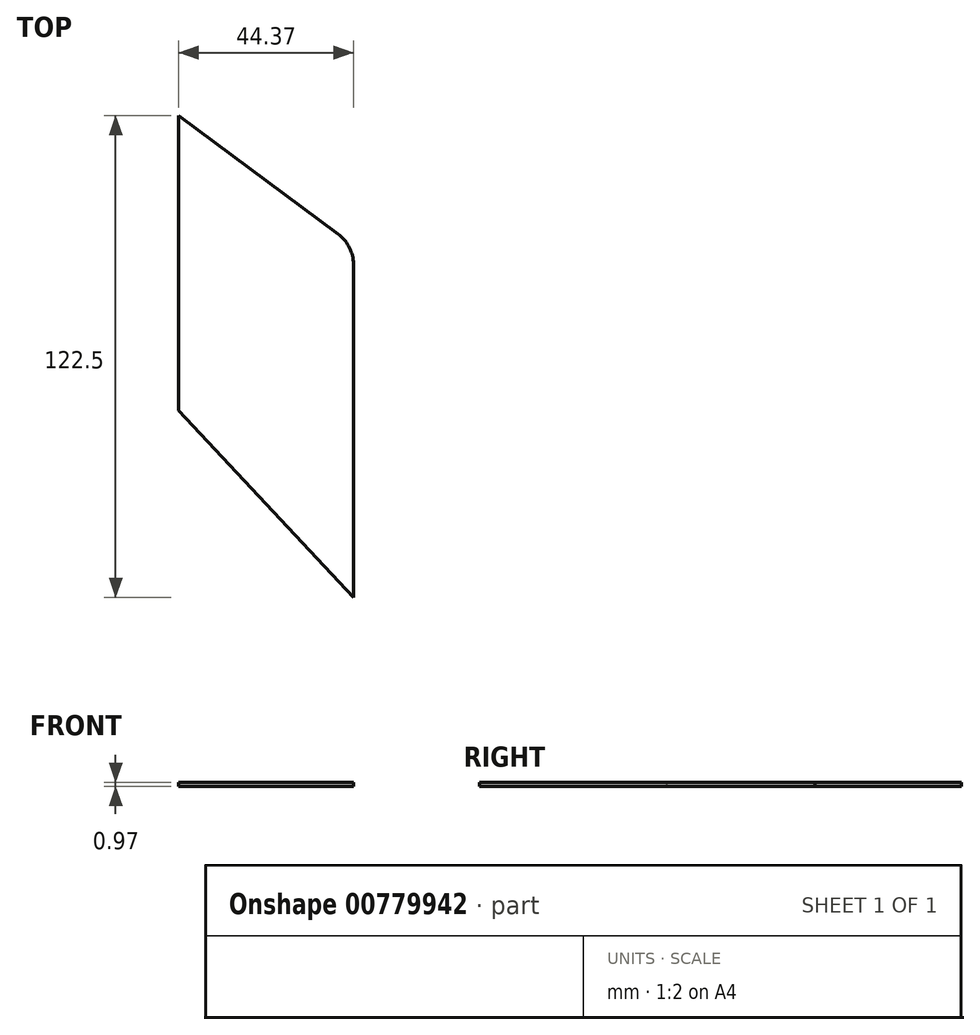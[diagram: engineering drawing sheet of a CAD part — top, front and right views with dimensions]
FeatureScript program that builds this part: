
annotation { "Feature Type Name" : "Feature", "Feature Type Description" : "" }
export const myFeature = defineFeature(function(context is Context, id is Id, definition is map)
    precondition{}
    {
        {
            var Q0;
            Q0=qCreatedBy(makeId("Top.planeOp"),FACE);
            var sketch = newSketch(context, id + "F0", { "sketchPlane" : qUnion([Q0])});
            skLineSegment(sketch, "E0", {"start": v(-38.1, 43.16) * mm, "end": v(-38.1, -31.84) * mm});
            skLineSegment(sketch, "E1", {"start": v(-38.1, -31.84) * mm, "end": v(6.26, -79.34) * mm});
            skLineSegment(sketch, "E2", {"start": v(6.26, -79.34) * mm, "end": v(6.26, 5.97) * mm});
            skLineSegment(sketch, "E3", {"start": v(2.38, 13.04) * mm, "end": v(-38.1, 43.16) * mm});
            skArc(sketch, "E4", {"start": v(6.26, 5.97) * mm, "mid": v(5.09, 9.93) * mm, "end": v(2.38, 13.04) * mm});
            skSolve(sketch);
        }
        {
            var Q0;
            Q0=makeQuery(id+"F0.imprint","IMPRINT",FACE,{"disambiguationData":[TD([[makeQuery(id+"F0.imprint","IMPRINT",EDGE,{"derivedFrom":sQuery(id+"F0.wireOp",EDGE,"E0")}),1.0]])]});
            extrude(context, id + "F1", {"entities" : qUnion([Q0]), "depth" : 0.97 * mm, "offsetDistance" : 25.4 * mm});
        }
    });
